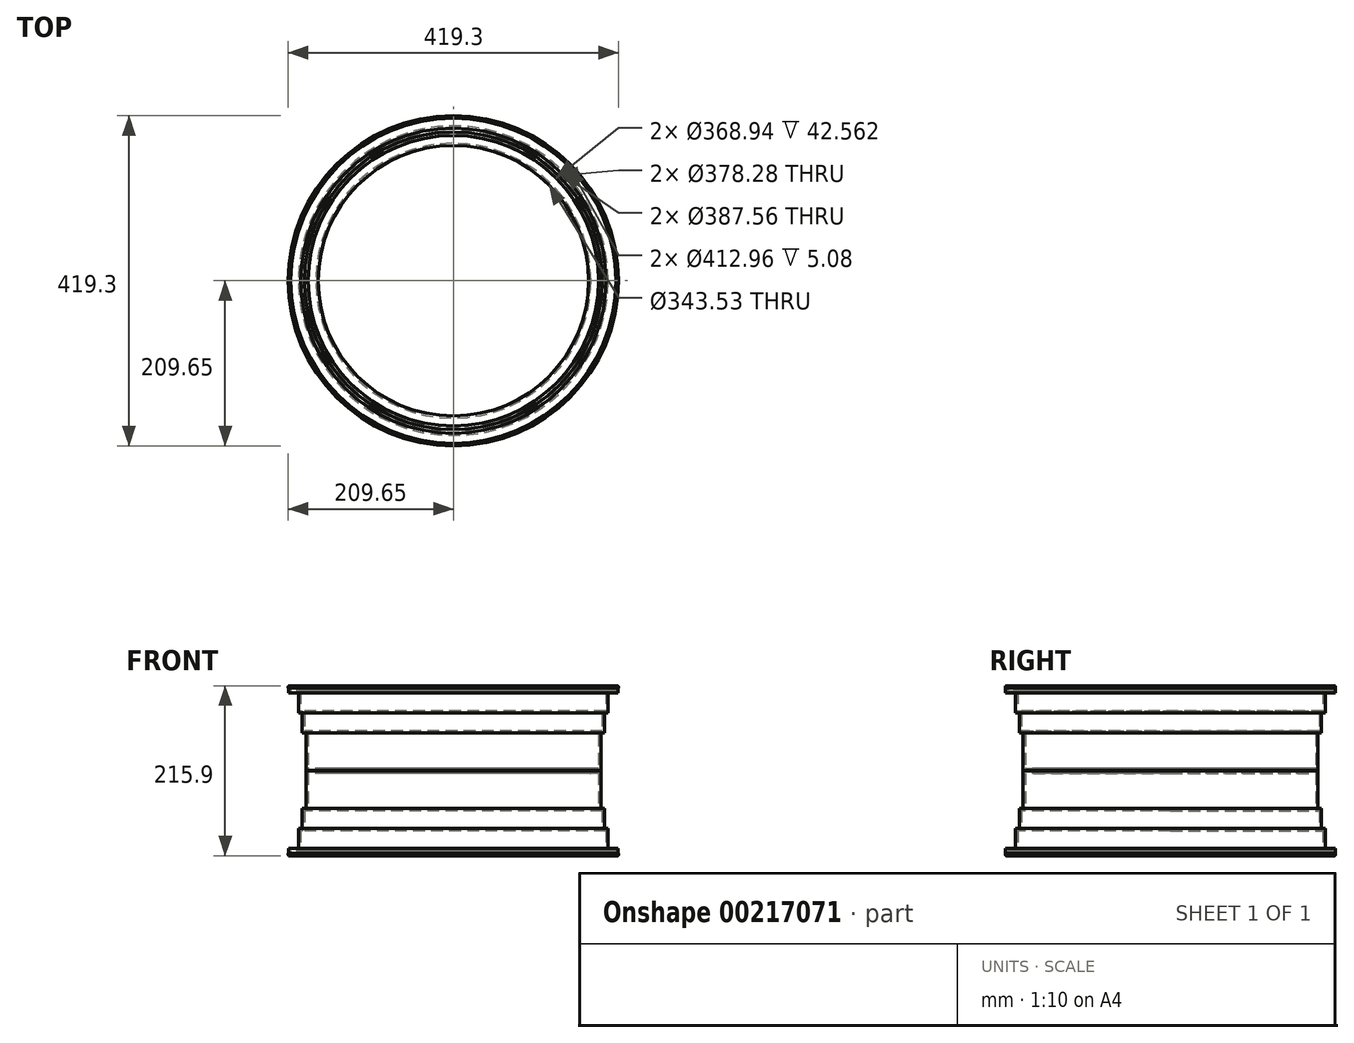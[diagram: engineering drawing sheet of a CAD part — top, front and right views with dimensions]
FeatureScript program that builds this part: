
annotation { "Feature Type Name" : "Feature", "Feature Type Description" : "" }
export const myFeature = defineFeature(function(context is Context, id is Id, definition is map)
    precondition{}
    {
        {
            var Q0;
            Q0=qCreatedBy(makeId("Top.planeOp"),FACE);
            var sketch = newSketch(context, id + "F0", { "sketchPlane" : qUnion([Q0])});
            skCircle(sketch, "E0", {"center": v(0, 0) * mm, "radius": 184.47 * mm});
            skCircle(sketch, "E1.0", {"center": v(0, 0) * mm, "radius": 171.77 * mm});
            skCircle(sketch, "E2", {"center": v(0, 0) * mm, "radius": 189.14 * mm});
            skCircle(sketch, "E3", {"center": v(0, 0) * mm, "radius": 193.78 * mm});
            skCircle(sketch, "E4.0", {"center": v(0, 0) * mm, "radius": 206.48 * mm});
            skCircle(sketch, "E5.0", {"center": v(0, 0) * mm, "radius": 209.65 * mm});
            skSolve(sketch);
        }
        {
            var Q0;
            Q0=makeQuery(id+"F0.imprint","IMPRINT",FACE,{"disambiguationData":[TD([[makeQuery(id+"F0.imprint","IMPRINT",EDGE,{"derivedFrom":sQuery(id+"F0.wireOp",EDGE,"E0")}),1.0]])]});
            var Q1;
            Q1=makeQuery(id+"F0.imprint","IMPRINT",FACE,{"disambiguationData":[TD([[makeQuery(id+"F0.imprint","IMPRINT",EDGE,{"derivedFrom":sQuery(id+"F0.wireOp",EDGE,"E0")}),-1.0]])]});
            extrude(context, id + "F1", {"entities" : qUnion([Q0, Q1]), "depth" : 6.35 * mm, "symmetric" : true});
        }
        {
            var Q0;
            Q0=makeQuery(id+"F0.imprint","IMPRINT",FACE,{"disambiguationData":[TD([[makeQuery(id+"F0.imprint","IMPRINT",EDGE,{"derivedFrom":sQuery(id+"F0.wireOp",EDGE,"E0")}),-1.0]])]});
            extrude(context, id + "F2", {"entities" : qUnion([Q0]), "operationType" : NewBodyOperationType.ADD, "depth" : 101.6 * mm, "symmetric" : true});
        }
        {
            var Q0;
            Q0=makeQuery(id+"F0.imprint","IMPRINT",FACE,{"disambiguationData":[TD([[makeQuery(id+"F0.imprint","IMPRINT",EDGE,{"derivedFrom":sQuery(id+"F0.wireOp",EDGE,"E2")}),-1.0]])]});
            extrude(context, id + "F3", {"entities" : qUnion([Q0]), "operationType" : NewBodyOperationType.ADD, "depth" : 152.4 * mm, "symmetric" : true});
        }
        {
            var Q0;
            Q0=makeQuery(id+"F0.imprint","IMPRINT",FACE,{"disambiguationData":[TD([[makeQuery(id+"F0.imprint","IMPRINT",EDGE,{"derivedFrom":sQuery(id+"F0.wireOp",EDGE,"E3")}),-1.0]])]});
            extrude(context, id + "F4", {"entities" : qUnion([Q0]), "operationType" : NewBodyOperationType.ADD, "depth" : 203.2 * mm, "symmetric" : true});
        }
        {
            var Q0;
            Q0=makeQuery(id+"F0.imprint","IMPRINT",FACE,{"disambiguationData":[TD([[makeQuery(id+"F0.imprint","IMPRINT",EDGE,{"derivedFrom":sQuery(id+"F0.wireOp",EDGE,"E4.0")}),-1.0]])]});
            extrude(context, id + "F5", {"entities" : qUnion([Q0]), "operationType" : NewBodyOperationType.ADD, "depth" : 215.9 * mm, "symmetric" : true});
        }
        {
            var Q0;
            Q0=makeQuery(id+"F5.opExtrude","SWEPT_FACE",FACE,{"disambiguationData":[OSD([sQuery(id+"F0.wireOp",EDGE,"E5.0")])]});
            shell(context, id + "F6", {"entities" : qUnion([Q0]), "thickness" : 2.86 * mm});
        }
        {
            var Q0;
            Q0=makeQuery(id+"F2.opExtrude","CAP_EDGE",EDGE,{"disambiguationData":[OSD([sQuery(id+"F0.wireOp",EDGE,"E0")])],"isStart":true});
            var Q1;
            Q1=makeQuery(id+"F3.opExtrude","CAP_EDGE",EDGE,{"disambiguationData":[OSD([sQuery(id+"F0.wireOp",EDGE,"E2")])],"isStart":true});
            fillet(context, id + "F7", {"entities" : qUnion([Q0, Q1]), "radius" : 5.08 * mm, "tangentPropagation" : true, "allowEdgeOverflow" : false});
        }
        {
            var Q0;
            Q0=makeQuery(id+"F1.opExtrude","CAP_EDGE",EDGE,{"disambiguationData":[OSD([sQuery(id+"F0.wireOp",EDGE,"E1.0")])],"isStart":true});
            fillet(context, id + "F8", {"entities" : qUnion([Q0]), "radius" : 2.54 * mm, "tangentPropagation" : true, "allowEdgeOverflow" : false});
        }
        {
            var Q0;
            Q0=makeQuery(id+"F1.opExtrude","CAP_EDGE",EDGE,{"disambiguationData":[OSD([sQuery(id+"F0.wireOp",EDGE,"E1.0")])],"isStart":false});
            fillet(context, id + "F9", {"entities" : qUnion([Q0]), "radius" : 2.54 * mm, "tangentPropagation" : true, "allowEdgeOverflow" : false});
        }
        {
            var Q0;
            Q0=makeQuery(id+"F2.opExtrude","CAP_EDGE",EDGE,{"disambiguationData":[OSD([sQuery(id+"F0.wireOp",EDGE,"E0")])],"isStart":false});
            var Q1;
            Q1=makeQuery(id+"F3.opExtrude","CAP_EDGE",EDGE,{"disambiguationData":[OSD([sQuery(id+"F0.wireOp",EDGE,"E2")])],"isStart":false});
            fillet(context, id + "F10", {"entities" : qUnion([Q0, Q1]), "radius" : 5.08 * mm, "tangentPropagation" : true, "allowEdgeOverflow" : false});
        }
        {
            var Q0;
            Q0=makeQuery(id+"F4.opExtrude","CAP_EDGE",EDGE,{"disambiguationData":[OSD([sQuery(id+"F0.wireOp",EDGE,"E3")])],"isStart":true});
            fillet(context, id + "F11", {"entities" : qUnion([Q0]), "radius" : 1.9 * mm, "tangentPropagation" : true, "allowEdgeOverflow" : false});
        }
        {
            var Q0;
            Q0=makeQuery(id+"F4.opExtrude","CAP_EDGE",EDGE,{"disambiguationData":[OSD([sQuery(id+"F0.wireOp",EDGE,"E3")])],"isStart":false});
            fillet(context, id + "F12", {"entities" : qUnion([Q0]), "radius" : 1.9 * mm, "tangentPropagation" : true, "allowEdgeOverflow" : false});
        }
        {
            var Q0;
            Q0=makeQuery(id+"F5.opExtrude","CAP_EDGE",EDGE,{"disambiguationData":[OSD([sQuery(id+"F0.wireOp",EDGE,"E4.0")])],"isStart":false});
            var Q1;
            Q1=makeQuery(id+"F5.opExtrude","CAP_EDGE",EDGE,{"disambiguationData":[OSD([sQuery(id+"F0.wireOp",EDGE,"E5.0")])],"isStart":false});
            var Q2;
            Q2=makeQuery(id+"F5.opExtrude","CAP_EDGE",EDGE,{"disambiguationData":[OSD([sQuery(id+"F0.wireOp",EDGE,"E5.0")])],"isStart":true});
            var Q3;
            Q3=makeQuery(id+"F5.opExtrude","CAP_EDGE",EDGE,{"disambiguationData":[OSD([sQuery(id+"F0.wireOp",EDGE,"E4.0")])],"isStart":true});
            fillet(context, id + "F13", {"entities" : qUnion([Q0, Q1, Q2, Q3]), "radius" : 1.27 * mm, "tangentPropagation" : true, "allowEdgeOverflow" : false});
        }
    });
